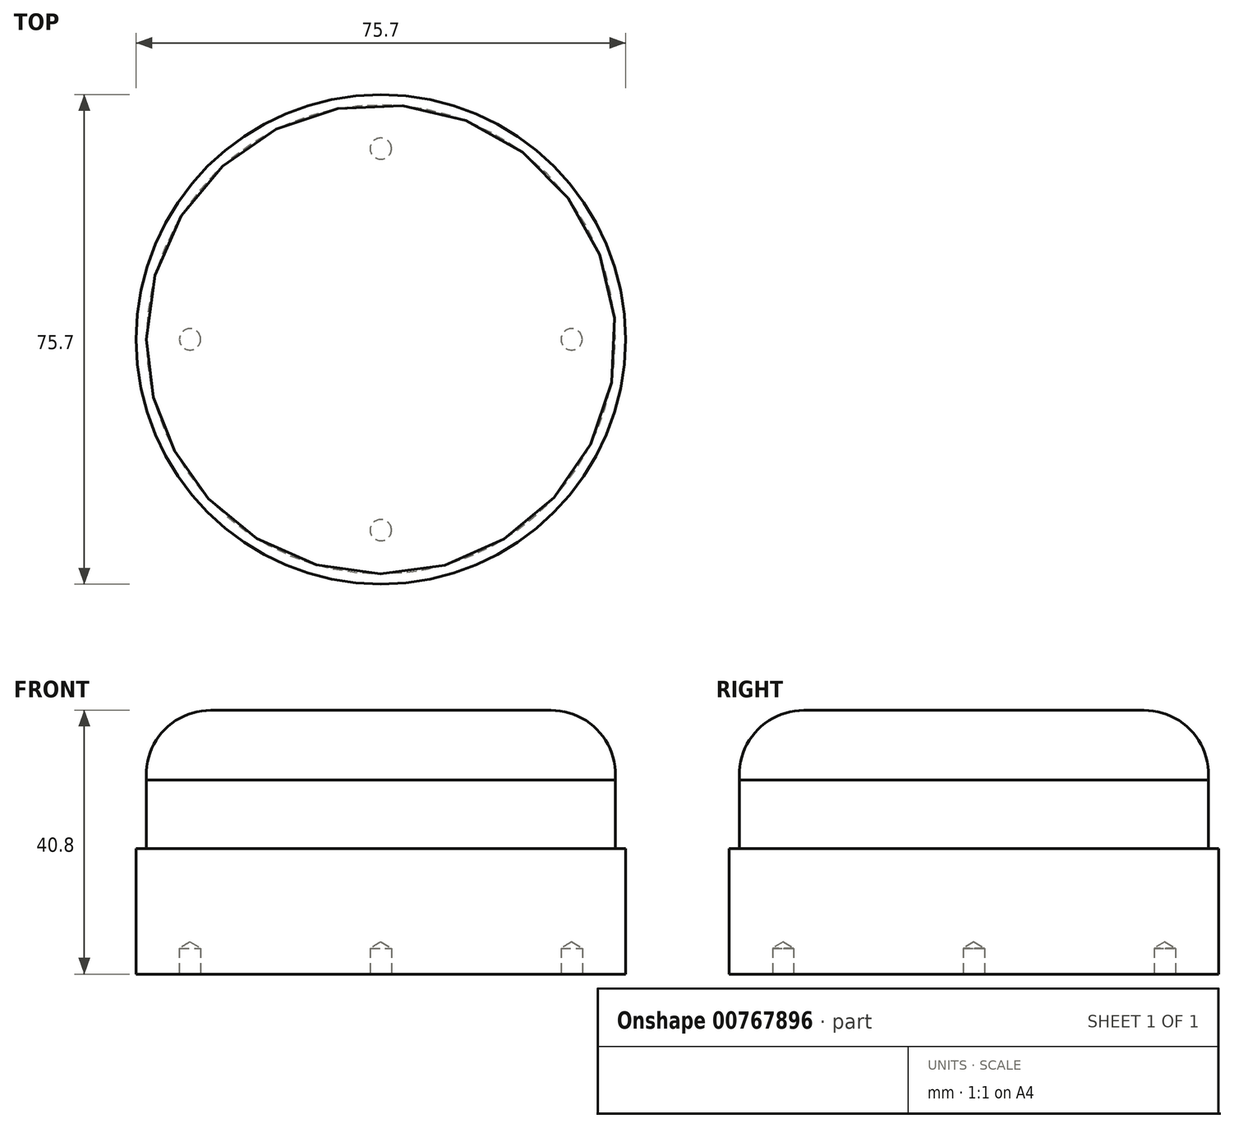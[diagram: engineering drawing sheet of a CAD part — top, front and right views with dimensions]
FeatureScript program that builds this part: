
annotation { "Feature Type Name" : "Feature", "Feature Type Description" : "" }
export const myFeature = defineFeature(function(context is Context, id is Id, definition is map)
    precondition{}
    {
        {
            var Q0;
            Q0=qCreatedBy(makeId("Top.planeOp"),FACE);
            var sketch = newSketch(context, id + "F0", { "sketchPlane" : qUnion([Q0])});
            skCircle(sketch, "E0", {"center": v(0, 0) * mm, "radius": 37.85 * mm});
            skSolve(sketch);
        }
        {
            var Q0;
            Q0 = qSketchRegion(id + "F0", true);
            extrude(context, id + "F1", {"entities" : qUnion([Q0]), "depth" : 19.4 * mm, "offsetDistance" : 25 * mm});
        }
        {
            var Q0;
            Q0=makeQuery(id+"F1.opExtrude","CAP_FACE",FACE,{"disambiguationData":[OSD([sQuery(id+"F0.wireOp",EDGE,"E0")])],"isStart":true});
            var sketch = newSketch(context, id + "F2", { "sketchPlane" : qUnion([Q0])});
            skCircle(sketch, "E1", {"center": v(0, 0) * mm, "radius": 29.5 * mm});
            skLineSegment(sketch, "E2", {"start": v(0, 35.24) * mm, "end": v(0, -34.54) * mm, "construction": true});
            skLineSegment(sketch, "E3", {"start": v(-33.06, 0) * mm, "end": v(34.77, 0) * mm, "construction": true});
            skPoint(sketch, "E4", {"position": v(0, 29.5) * mm});
            skPoint(sketch, "E5", {"position": v(-29.5, 0) * mm});
            skPoint(sketch, "E6", {"position": v(29.5, 0) * mm});
            skPoint(sketch, "E7", {"position": v(0, -29.5) * mm});
            skSolve(sketch);
        }
        {
            var Q0;
            Q0=sQuery(id+"F2.wireOp",VERTEX,"E4");
            var Q1;
            Q1=sQuery(id+"F2.wireOp",VERTEX,"E5");
            var Q2;
            Q2=sQuery(id+"F2.wireOp",VERTEX,"E7");
            var Q3;
            Q3=sQuery(id+"F2.wireOp",VERTEX,"E6");
            var Q4;
            Q4=makeQuery(id+"F1.opExtrude","SWEPT_BODY",BODY,{"disambiguationData":[OSD([sQuery(id+"F0.wireOp",EDGE,"E0")])]});
            hole(context, id + "F3", {"style" : HoleStyle.SIMPLE, "endStyle" : HoleEndStyle.BLIND, "standardTappedOrClearance" : lookupTablePath({ "standard" : "ISO", "fit" : "Normal", "size" : "M3", "type" : "Clearance" }), "standardBlindInLast" : lookupTablePath({ "fit" : "Standard", "standard" : "ISO", "size" : "M3", "type" : "Clearance" }), "holeDiameter" : 3.3 * mm, "majorDiameter" : 5 * mm, "holeDepth" : 4 * mm, "isTappedThrough" : true, "tappedDepth" : 12 * mm, "tapClearance" : 3, "locations" : qUnion([Q0, Q1, Q2, Q3]), "scope" : qUnion([Q4])});
        }
        {
            var Q0;
            Q0=qCreatedBy(makeId("Right.planeOp"),FACE);
            var sketch = newSketch(context, id + "F4", { "sketchPlane" : qUnion([Q0])});
            skLineSegment(sketch, "E8.0.0", {"start": v(-37.85, 19.4) * mm, "end": v(37.85, 19.4) * mm});
            skLineSegment(sketch, "E9", {"start": v(0, 19.4) * mm, "end": v(0, 40.8) * mm});
            skLineSegment(sketch, "E10", {"start": v(0, 40.8) * mm, "end": v(-26.28, 40.8) * mm});
            skPoint(sketch, "E11.visualSharp", {"position": v(-36.25, 40.8) * mm});
            skArc(sketch, "E11.filletArc", {"start": v(-26.28, 40.8) * mm, "mid": v(-33.64, 37.58) * mm, "end": v(-36.25, 29.98) * mm});
            skLineSegment(sketch, "E12", {"start": v(0, 19.4) * mm, "end": v(-36.25, 19.4) * mm});
            skLineSegment(sketch, "E13", {"start": v(-36.25, 19.4) * mm, "end": v(-36.25, 29.98) * mm});
            skSolve(sketch);
        }
        {
            var Q0;
            Q0=makeQuery(id+"F4.imprint","IMPRINT",FACE,{"disambiguationData":[TD([[makeQuery(id+"F4.imprint","IMPRINT",EDGE,{"derivedFrom":sQuery(id+"F4.wireOp",EDGE,"E9")}),1.0]])]});
            var Q1;
            Q1=sQuery(id+"F4.wireOp",EDGE,"E9");
            revolve(context, id + "F5", {"operationType" : NewBodyOperationType.ADD, "surfaceOperationType" : NewSurfaceOperationType.NEW, "entities" : qUnion([Q0]), "axis" : qUnion([Q1]), "revolveType" : RevolveType.FULL});
        }
    });
